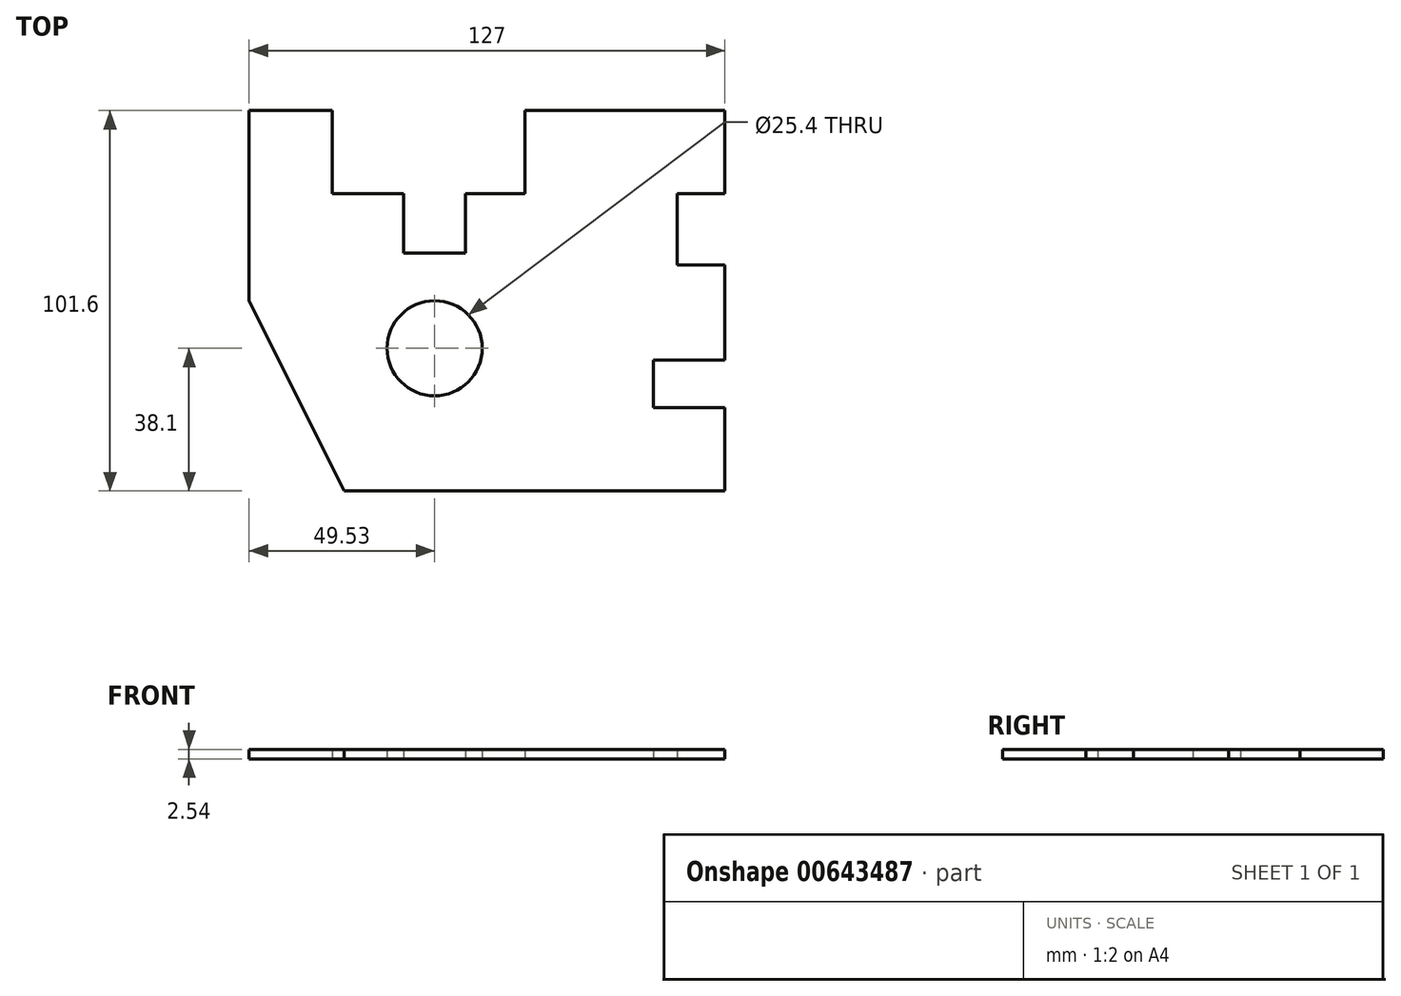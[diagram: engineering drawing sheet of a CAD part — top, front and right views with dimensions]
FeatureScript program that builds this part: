
annotation { "Feature Type Name" : "Feature", "Feature Type Description" : "" }
export const myFeature = defineFeature(function(context is Context, id is Id, definition is map)
    precondition{}
    {
        {
            var Q0;
            Q0=qCreatedBy(makeId("Top.planeOp"),FACE);
            var sketch = newSketch(context, id + "F0", { "sketchPlane" : qUnion([Q0])});
            skLineSegment(sketch, "E0.bottom", {"start": v(25.4, 0) * mm, "end": v(127, 0) * mm});
            skLineSegment(sketch, "E0.top", {"start": v(0, 101.6) * mm, "end": v(22.22, 101.6) * mm});
            skLineSegment(sketch, "E0.left", {"start": v(0, 50.8) * mm, "end": v(0, 101.6) * mm});
            skLineSegment(sketch, "E0.right", {"start": v(127, 0) * mm, "end": v(127, 22.23) * mm});
            skLineSegment(sketch, "E1", {"start": v(0, 50.8) * mm, "end": v(25.4, 0) * mm});
            skPoint(sketch, "E2.orphan", {"position": v(0, 0) * mm});
            skPoint(sketch, "E3.right.start.orphan", {"position": v(25.4, 50.8) * mm});
            skCircle(sketch, "E4", {"center": v(49.53, 38.1) * mm, "radius": 12.7 * mm});
            skLineSegment(sketch, "E5.right", {"start": v(22.22, 79.38) * mm, "end": v(22.22, 101.6) * mm});
            skLineSegment(sketch, "E6.top", {"start": v(49.53, 63.5) * mm, "end": v(57.78, 63.5) * mm});
            skLineSegment(sketch, "E7.top", {"start": v(57.78, 79.38) * mm, "end": v(73.66, 79.38) * mm});
            skLineSegment(sketch, "E7.left", {"start": v(57.78, 63.5) * mm, "end": v(57.78, 79.38) * mm});
            skLineSegment(sketch, "E8", {"start": v(73.66, 79.38) * mm, "end": v(73.66, 101.6) * mm});
            skPoint(sketch, "E7.bottom.end.orphan", {"position": v(73.66, 63.5) * mm});
            skLineSegment(sketch, "E9.MirrorCS", {"start": v(41.27, 63.5) * mm, "end": v(41.27, 79.38) * mm});
            skLineSegment(sketch, "E10.MirrorCS", {"start": v(49.53, 63.5) * mm, "end": v(41.27, 63.5) * mm});
            skLineSegment(sketch, "E11", {"start": v(41.27, 79.38) * mm, "end": v(22.22, 79.38) * mm});
            skPoint(sketch, "E6.bottom.end.orphan", {"position": v(57.79, 38.1) * mm});
            skLineSegment(sketch, "E12.trimOffspring", {"start": v(73.66, 101.6) * mm, "end": v(127, 101.6) * mm});
            skLineSegment(sketch, "E13.bottom", {"start": v(127, 0) * mm, "end": v(107.95, 0) * mm});
            skLineSegment(sketch, "E13.top", {"start": v(127, 22.23) * mm, "end": v(107.95, 22.23) * mm});
            skLineSegment(sketch, "E14.bottom", {"start": v(107.95, 22.23) * mm, "end": v(127, 22.23) * mm});
            skLineSegment(sketch, "E14.top", {"start": v(107.95, 34.93) * mm, "end": v(127, 34.93) * mm});
            skLineSegment(sketch, "E14.left", {"start": v(107.95, 22.23) * mm, "end": v(107.95, 34.93) * mm});
            skLineSegment(sketch, "E15.trimOffspring", {"start": v(127, 34.93) * mm, "end": v(127, 60.33) * mm});
            skLineSegment(sketch, "E16.bottom", {"start": v(127, 34.93) * mm, "end": v(114.3, 34.93) * mm});
            skLineSegment(sketch, "E16.top", {"start": v(127, 60.33) * mm, "end": v(114.3, 60.33) * mm});
            skLineSegment(sketch, "E17.bottom", {"start": v(114.3, 60.33) * mm, "end": v(127, 60.33) * mm});
            skLineSegment(sketch, "E17.top", {"start": v(114.3, 79.38) * mm, "end": v(127, 79.38) * mm});
            skLineSegment(sketch, "E17.left", {"start": v(114.3, 60.33) * mm, "end": v(114.3, 79.38) * mm});
            skLineSegment(sketch, "E18.trimOffspring", {"start": v(127, 79.38) * mm, "end": v(127, 101.6) * mm});
            skSolve(sketch);
        }
        {
            var Q0;
            Q0=makeQuery(id+"F0.imprint","IMPRINT",FACE,{"disambiguationData":[TD([[makeQuery(id+"F0.imprint","IMPRINT",EDGE,{"derivedFrom":sQuery(id+"F0.wireOp",EDGE,"E0.bottom")}),1.0]])]});
            extrude(context, id + "F1", {"entities" : qUnion([Q0]), "depth" : 2.54 * mm, "offsetDistance" : 25.4 * mm});
        }
    });
